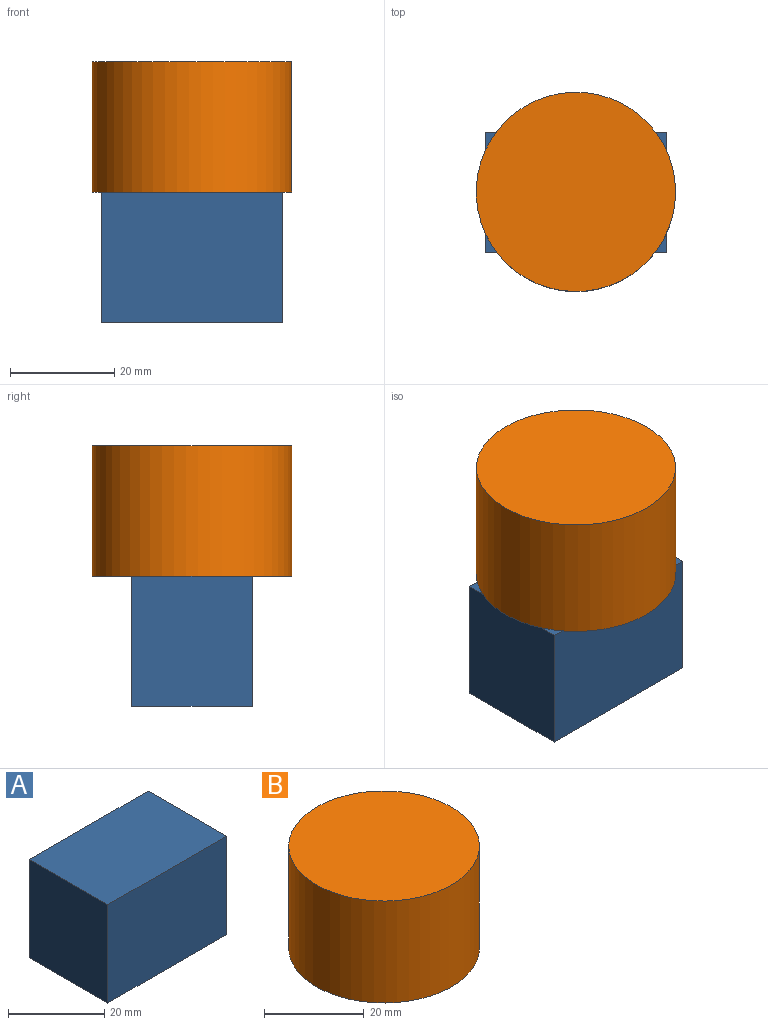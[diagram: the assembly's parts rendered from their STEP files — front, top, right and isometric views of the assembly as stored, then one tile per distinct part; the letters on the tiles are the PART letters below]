
ASSEMBLY  parts=2 mates=1
PART A: 6 faces, bbox 34.8x23x25 mm
  f0: plane 34.85x25mm, normal (0,1,0), area 871.2mm2, adj f1,f3,f4,f5
  f1: plane 25x23.01mm, normal (-1,0,0), area 575.2mm2, adj f0,f2,f4,f5
  f2: plane 34.85x25mm, normal (0,-1,0), area 871.2mm2, adj f1,f3,f4,f5
  f3: plane 25x23.01mm, normal (1,0,0), area 575.2mm2, adj f0,f2,f4,f5
  f4: plane 34.85x23.01mm, normal (0,0,1), area 801.7mm2, adj f0,f1,f2,f3
  f5: plane 34.85x23.01mm, normal (0,0,-1), area 801.7mm2, adj f0,f1,f2,f3
PART B: 3 faces, bbox 38.2x38.2x25 mm
  f0: cylinder r=19.1mm len=38.2mm, axis (0,0,-1), area 3000.3mm2, adj f1,f2
  f1: plane 38.2x38.2mm, normal (0,0,1), area 1146.1mm2, adj f0
  f2: plane 38.2x38.2mm, normal (0,0,-1), area 1146.1mm2, adj f0
PLACE A t=(-17.41,11.4,-12.66)mm
PLACE B t=(0.02,-0.1,12.34)mm
MATE fastened B.f0 <-> A.f4  axis (0,0,-1) through (0.02,-0.1,12.34)mm
